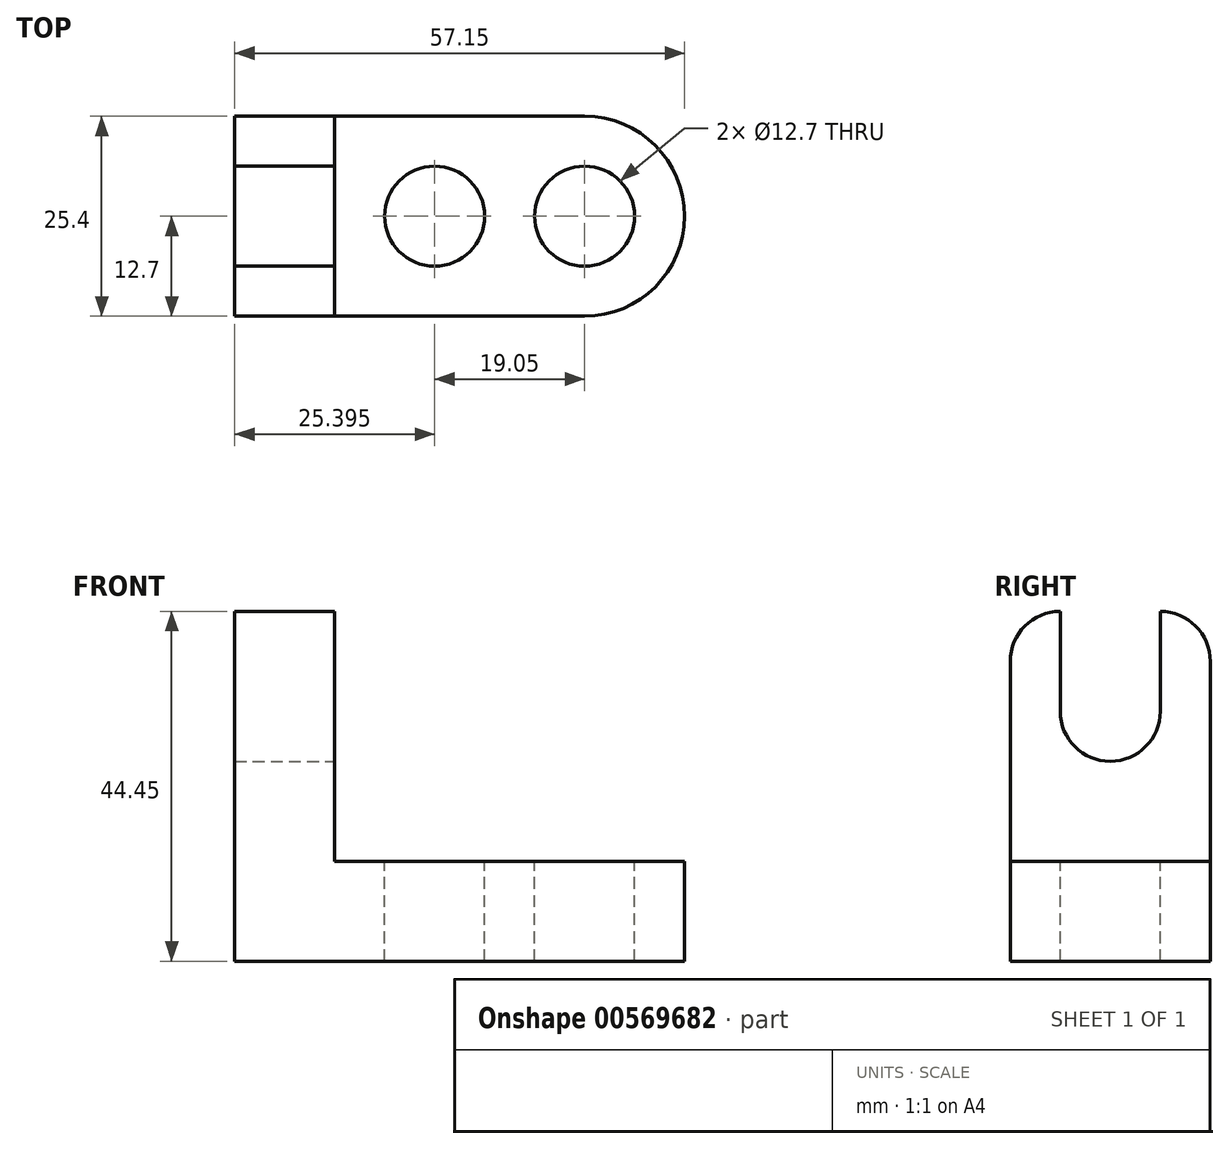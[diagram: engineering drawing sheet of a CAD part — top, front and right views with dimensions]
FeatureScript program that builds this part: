
annotation { "Feature Type Name" : "Feature", "Feature Type Description" : "" }
export const myFeature = defineFeature(function(context is Context, id is Id, definition is map)
    precondition{}
    {
        {
            var Q0;
            Q0=qCreatedBy(makeId("Top.planeOp"),FACE);
            var sketch = newSketch(context, id + "F0", { "sketchPlane" : qUnion([Q0])});
            skLineSegment(sketch, "E0.bottom", {"start": v(-15.04, -12.7) * mm, "end": v(42.1, -12.7) * mm});
            skLineSegment(sketch, "E0.top", {"start": v(-15.04, 12.7) * mm, "end": v(42.1, 12.7) * mm});
            skLineSegment(sketch, "E0.left", {"start": v(-15.04, -12.7) * mm, "end": v(-15.04, 12.7) * mm});
            skLineSegment(sketch, "E0.right", {"start": v(42.1, -12.7) * mm, "end": v(42.1, 12.7) * mm});
            skSolve(sketch);
        }
        {
            var Q0;
            Q0 = qSketchRegion(id + "F0", true);
            extrude(context, id + "F1", {"entities" : qUnion([Q0]), "depth" : 44.45 * mm, "offsetDistance" : 25.4 * mm});
        }
        {
            var Q0;
            Q0=makeQuery(id+"F1.opExtrude","SWEPT_FACE",FACE,{"disambiguationData":[OSD([sQuery(id+"F0.wireOp",EDGE,"E0.bottom")])]});
            var sketch = newSketch(context, id + "F2", { "sketchPlane" : qUnion([Q0])});
            skLineSegment(sketch, "E1", {"start": v(-2.34, 44.45) * mm, "end": v(-2.34, 12.7) * mm});
            skLineSegment(sketch, "E2", {"start": v(-2.34, 12.7) * mm, "end": v(42.1, 12.7) * mm});
            skLineSegment(sketch, "E3", {"start": v(42.1, 12.7) * mm, "end": v(42.1, 44.45) * mm});
            skLineSegment(sketch, "E4", {"start": v(42.1, 44.45) * mm, "end": v(-2.34, 44.45) * mm});
            skSolve(sketch);
        }
        {
            var Q0;
            Q0 = qSketchRegion(id + "F2", true);
            extrude(context, id + "F3", {"entities" : qUnion([Q0]), "operationType" : NewBodyOperationType.REMOVE, "oppositeDirection" : true, "depth" : 25.4 * mm, "offsetDistance" : 25.4 * mm});
        }
        {
            var Q0;
            Q0=makeQuery(id+"F3.boolean.opBoolean","COPY",FACE,{"derivedFrom":makeQuery(id+"F3.opExtrude","SWEPT_FACE",FACE,{"disambiguationData":[OSD([sQuery(id+"F2.wireOp",EDGE,"E1")])]})});
            var sketch = newSketch(context, id + "F4", { "sketchPlane" : qUnion([Q0])});
            skLineSegment(sketch, "E5", {"start": v(-12.7, 44.45) * mm, "end": v(-12.7, 31.75) * mm});
            skArc(sketch, "E6", {"start": v(-6.35, 31.75) * mm, "mid": v(0, 25.4) * mm, "end": v(6.35, 31.75) * mm});
            skLineSegment(sketch, "E7", {"start": v(-6.35, 31.75) * mm, "end": v(-6.35, 44.45) * mm});
            skLineSegment(sketch, "E8", {"start": v(-6.35, 44.45) * mm, "end": v(6.35, 44.45) * mm});
            skLineSegment(sketch, "E9", {"start": v(6.35, 44.45) * mm, "end": v(6.35, 31.75) * mm});
            skPoint(sketch, "E10.orphan", {"position": v(12.7, 31.75) * mm});
            skPoint(sketch, "E11.orphan", {"position": v(0, 44.45) * mm});
            skPoint(sketch, "E12.end.orphan", {"position": v(0, 12.7) * mm});
            skPoint(sketch, "E13.start.orphan", {"position": v(0, 25.4) * mm});
            skSolve(sketch);
        }
        {
            var Q0;
            Q0 = qSketchRegion(id + "F4", true);
            extrude(context, id + "F5", {"entities" : qUnion([Q0]), "operationType" : NewBodyOperationType.REMOVE, "oppositeDirection" : true, "depth" : 25.4 * mm, "offsetDistance" : 25.4 * mm});
        }
        {
            var Q0;
            Q0=makeQuery(id+"F3.boolean.opBoolean","COPY",FACE,{"derivedFrom":makeQuery(id+"F3.opExtrude","SWEPT_FACE",FACE,{"disambiguationData":[OSD([sQuery(id+"F2.wireOp",EDGE,"E1")])]})});
            var sketch = newSketch(context, id + "F6", { "sketchPlane" : qUnion([Q0])});
            skArc(sketch, "E14", {"start": v(-6.35, 44.45) * mm, "mid": v(-10.84, 42.6) * mm, "end": v(-12.7, 38.1) * mm});
            skArc(sketch, "E15", {"start": v(12.7, 38.1) * mm, "mid": v(10.84, 42.6) * mm, "end": v(6.35, 44.45) * mm});
            skSolve(sketch);
        }
        {
            var Q0;
            {var subQ0=sQuery(id+"F6.wireOp",EDGE,"E15");Q0=makeQuery(id+"F6.imprint","IMPRINT",FACE,{"disambiguationData":[TD([[makeQuery(id+"F6.imprint","IMPRINT",EDGE,{"derivedFrom":subQ0}),-1.0]])]});}
            var Q1;
            {var subQ0=sQuery(id+"F6.wireOp",EDGE,"E14");Q1=makeQuery(id+"F6.imprint","IMPRINT",FACE,{"disambiguationData":[TD([[makeQuery(id+"F6.imprint","IMPRINT",EDGE,{"derivedFrom":subQ0}),-1.0]])]});}
            extrude(context, id + "F7", {"entities" : qUnion([Q0, Q1]), "operationType" : NewBodyOperationType.REMOVE, "oppositeDirection" : true, "depth" : 25.4 * mm, "offsetDistance" : 25.4 * mm});
        }
        {
            var Q0;
            Q0=makeQuery(id+"F3.boolean.opBoolean","COPY",FACE,{"derivedFrom":makeQuery(id+"F3.opExtrude","SWEPT_FACE",FACE,{"disambiguationData":[OSD([sQuery(id+"F2.wireOp",EDGE,"E2")])]})});
            var sketch = newSketch(context, id + "F8", { "sketchPlane" : qUnion([Q0])});
            skLineSegment(sketch, "E16", {"start": v(29.4, 6.35) * mm, "end": v(29.4, 0) * mm});
            skCircle(sketch, "E17", {"center": v(29.4, 0) * mm, "radius": 6.35 * mm});
            skLineSegment(sketch, "E18", {"start": v(10.36, 6.35) * mm, "end": v(10.36, 0) * mm});
            skCircle(sketch, "E19", {"center": v(10.36, 0) * mm, "radius": 6.35 * mm});
            skPoint(sketch, "E20.orphan", {"position": v(29.4, -12.7) * mm});
            skPoint(sketch, "E21.orphan", {"position": v(29.4, 12.7) * mm});
            skPoint(sketch, "E22.orphan", {"position": v(10.36, -12.7) * mm});
            skPoint(sketch, "E23.end.orphan", {"position": v(10.36, 12.7) * mm});
            skSolve(sketch);
        }
        {
            var Q0;
            Q0 = qSketchRegion(id + "F8", true);
            extrude(context, id + "F9", {"entities" : qUnion([Q0]), "operationType" : NewBodyOperationType.REMOVE, "oppositeDirection" : true, "depth" : 25.4 * mm, "offsetDistance" : 25.4 * mm});
        }
        {
            var Q0;
            Q0=makeQuery(id+"F3.boolean.opBoolean","COPY",FACE,{"derivedFrom":makeQuery(id+"F3.opExtrude","SWEPT_FACE",FACE,{"disambiguationData":[OSD([sQuery(id+"F2.wireOp",EDGE,"E2")])]})});
            var sketch = newSketch(context, id + "F10", { "sketchPlane" : qUnion([Q0])});
            skArc(sketch, "E24", {"start": v(29.4, -12.7) * mm, "mid": v(42.1, 0) * mm, "end": v(29.4, 12.7) * mm});
            skSolve(sketch);
        }
        {
            var Q0;
            {var subQ0=sQuery(id+"F10.wireOp",EDGE,"E24");var subQ1=sQuery(id+"F2.wireOp",EDGE,"E2");var subQ2=makeQuery(id+"F3.boolean.opBoolean","COPY",EDGE,{"derivedFrom":makeQuery(id+"F3.opExtrude","CAP_EDGE",EDGE,{"disambiguationData":[OSD([subQ1])],"isStart":false})});var subQ3=makeQuery(id+"F10.imprint","INTERSECT",VERTEX,{"derivedFrom":[subQ2,subQ0]});Q0=makeQuery(id+"F10.imprint","IMPRINT",FACE,{"disambiguationData":[TD([[makeQuery(id+"F10.imprint","IMPRINT",EDGE,{"disambiguationData":[TD([[subQ3,1.0]])],"derivedFrom":subQ0}),-1.0]])]});}
            var Q1;
            {var subQ0=sQuery(id+"F10.wireOp",EDGE,"E24");var subQ1=sQuery(id+"F2.wireOp",EDGE,"E2");var subQ2=makeQuery(id+"F3.boolean.opBoolean","COPY",EDGE,{"derivedFrom":makeQuery(id+"F3.opExtrude","CAP_EDGE",EDGE,{"disambiguationData":[OSD([subQ1])],"isStart":true})});var subQ3=makeQuery(id+"F10.imprint","INTERSECT",VERTEX,{"derivedFrom":[subQ2,subQ0]});Q1=makeQuery(id+"F10.imprint","IMPRINT",FACE,{"disambiguationData":[TD([[makeQuery(id+"F10.imprint","IMPRINT",EDGE,{"disambiguationData":[TD([[subQ3,-1.0]])],"derivedFrom":subQ0}),-1.0]])]});}
            extrude(context, id + "F11", {"entities" : qUnion([Q0, Q1]), "operationType" : NewBodyOperationType.REMOVE, "oppositeDirection" : true, "depth" : 25.4 * mm, "offsetDistance" : 25.4 * mm});
        }
    });
